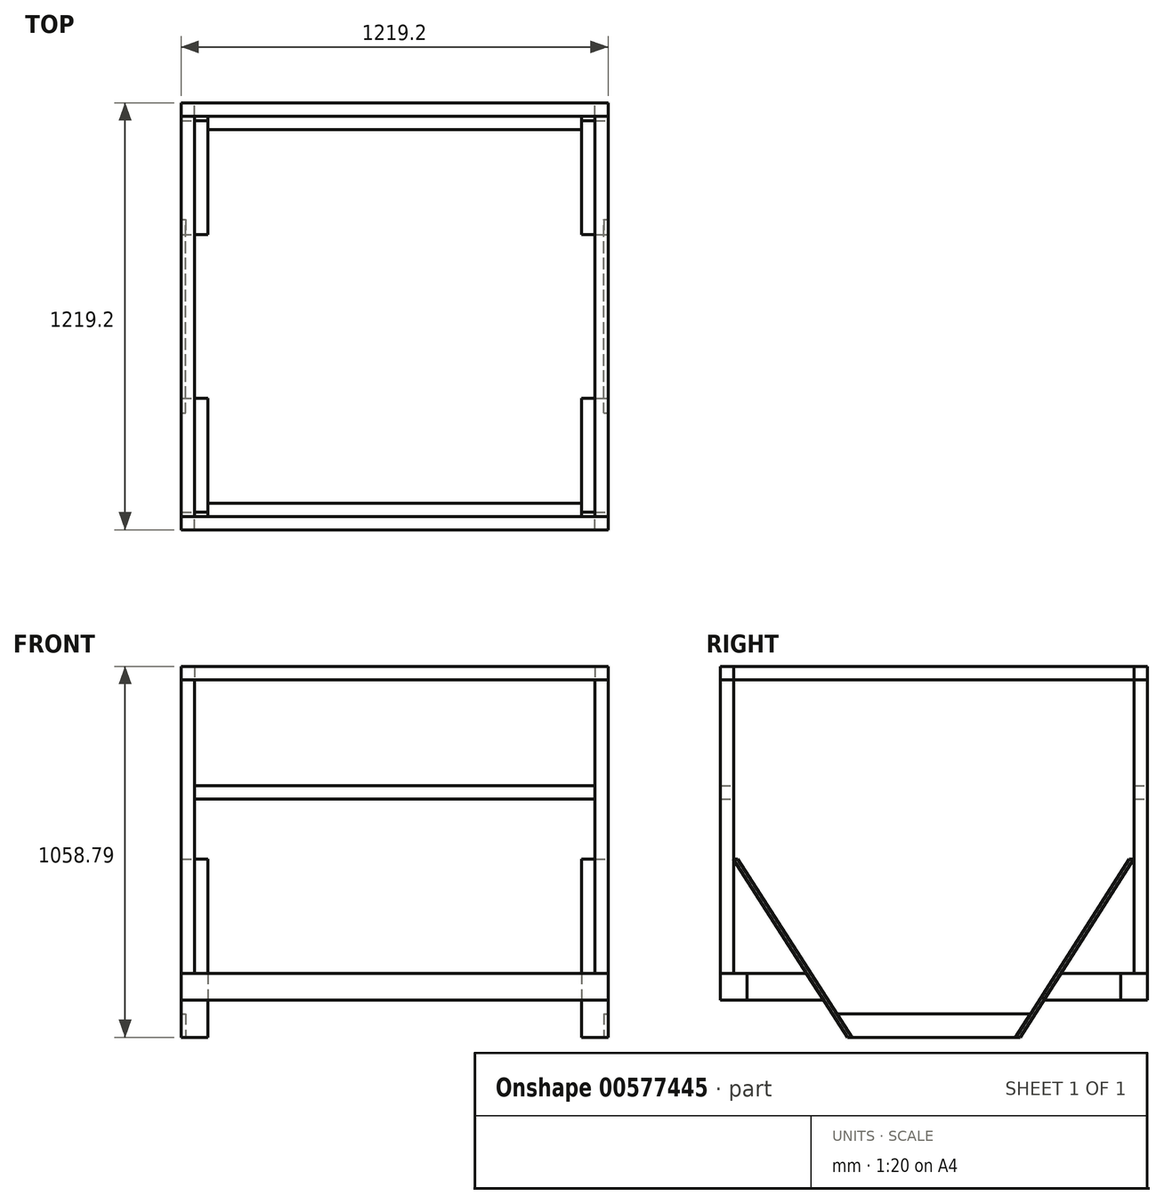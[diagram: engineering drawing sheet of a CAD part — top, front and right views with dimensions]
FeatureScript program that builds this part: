
annotation { "Feature Type Name" : "Feature", "Feature Type Description" : "" }
export const myFeature = defineFeature(function(context is Context, id is Id, definition is map)
    precondition{}
    {
        {
            var Q0;
            Q0=qCreatedBy(makeId("Front.planeOp"),FACE);
            var sketch = newSketch(context, id + "F0", { "sketchPlane" : qUnion([Q0])});
            skLineSegment(sketch, "E0.bottom", {"start": v(-609.6, 38.1) * mm, "end": v(609.6, 38.1) * mm});
            skLineSegment(sketch, "E0.top", {"start": v(-609.6, -38.1) * mm, "end": v(609.6, -38.1) * mm});
            skLineSegment(sketch, "E0.left", {"start": v(-609.6, 38.1) * mm, "end": v(-609.6, -38.1) * mm});
            skLineSegment(sketch, "E0.right", {"start": v(609.6, 38.1) * mm, "end": v(609.6, -38.1) * mm});
            skPoint(sketch, "E0.middle", {"position": v(0, 0) * mm});
            skSolve(sketch);
        }
        {
            var Q0;
            Q0=makeQuery(id+"F0.imprint","IMPRINT",FACE,{"disambiguationData":[TD([[makeQuery(id+"F0.imprint","IMPRINT",EDGE,{"derivedFrom":sQuery(id+"F0.wireOp",EDGE,"E0.bottom")}),-1.0]])]});
            extrude(context, id + "F1", {"entities" : qUnion([Q0]), "depth" : 76.2 * mm, "offsetDistance" : 25.4 * mm});
        }
        {
            var Q0;
            Q0=qCreatedBy(makeId("Front.planeOp"),FACE);
            var sketch = newSketch(context, id + "F2", { "sketchPlane" : qUnion([Q0])});
            skLineSegment(sketch, "E1.bottom", {"start": v(-609.6, 911.23) * mm, "end": v(609.6, 911.23) * mm});
            skLineSegment(sketch, "E1.top", {"start": v(-609.6, 873.12) * mm, "end": v(609.6, 873.12) * mm});
            skLineSegment(sketch, "E1.left", {"start": v(-609.6, 911.23) * mm, "end": v(-609.6, 873.12) * mm});
            skLineSegment(sketch, "E1.right", {"start": v(609.6, 911.23) * mm, "end": v(609.6, 873.12) * mm});
            skPoint(sketch, "E1.middle", {"position": v(0, 892.18) * mm});
            skSolve(sketch);
        }
        {
            var Q0;
            Q0=makeQuery(id+"F2.imprint","IMPRINT",FACE,{"disambiguationData":[TD([[makeQuery(id+"F2.imprint","IMPRINT",EDGE,{"derivedFrom":sQuery(id+"F2.wireOp",EDGE,"E1.bottom")}),-1.0]])]});
            extrude(context, id + "F3", {"entities" : qUnion([Q0]), "depth" : 38.1 * mm, "offsetDistance" : 25.4 * mm});
        }
        {
            var Q0;
            Q0=qCreatedBy(makeId("Front.planeOp"),FACE);
            var sketch = newSketch(context, id + "F4", { "sketchPlane" : qUnion([Q0])});
            skLineSegment(sketch, "E2.bottom", {"start": v(609.6, 876.3) * mm, "end": v(571.5, 876.3) * mm});
            skLineSegment(sketch, "E2.top", {"start": v(609.6, 38.1) * mm, "end": v(571.5, 38.1) * mm});
            skLineSegment(sketch, "E2.left", {"start": v(609.6, 876.3) * mm, "end": v(609.6, 38.1) * mm});
            skLineSegment(sketch, "E2.right", {"start": v(571.5, 876.3) * mm, "end": v(571.5, 38.1) * mm});
            skPoint(sketch, "E2.middle", {"position": v(590.55, 457.2) * mm});
            skSolve(sketch);
        }
        {
            var Q0;
            Q0=makeQuery(id+"F4.imprint","IMPRINT",FACE,{"disambiguationData":[TD([[makeQuery(id+"F4.imprint","IMPRINT",EDGE,{"derivedFrom":sQuery(id+"F4.wireOp",EDGE,"E2.bottom")}),1.0]])]});
            extrude(context, id + "F5", {"entities" : qUnion([Q0]), "depth" : 38.1 * mm, "offsetDistance" : 25.4 * mm});
        }
        {
            var Q0;
            Q0=makeQuery(id+"F5.opExtrude","SWEPT_BODY",BODY,{"disambiguationData":[OSD([sQuery(id+"F4.wireOp",EDGE,"E2.bottom"),sQuery(id+"F4.wireOp",EDGE,"E2.top"),sQuery(id+"F4.wireOp",EDGE,"E2.left"),sQuery(id+"F4.wireOp",EDGE,"E2.right")])]});
            var Q1;
            Q1=qCreatedBy(makeId("Right.planeOp"),FACE);
            transform(context, id + "F6", {"entities" : qUnion([Q0]), "transformType" : TransformType.TRANSLATION_DISTANCE, "transformDirection" : qUnion([Q1]), "distance" : 1181.1 * mm, "oppositeDirection" : true, "makeCopy" : true});
        }
        {
            var Q0;
            Q0=makeQuery(id+"F3.opExtrude","SWEPT_BODY",BODY,{"disambiguationData":[OSD([sQuery(id+"F2.wireOp",EDGE,"E1.bottom"),sQuery(id+"F2.wireOp",EDGE,"E1.top"),sQuery(id+"F2.wireOp",EDGE,"E1.left"),sQuery(id+"F2.wireOp",EDGE,"E1.right")])]});
            var Q1;
            Q1=qCreatedBy(makeId("Top.planeOp"),FACE);
            transform(context, id + "F7", {"entities" : qUnion([Q0]), "transformType" : TransformType.TRANSLATION_DISTANCE, "transformDirection" : qUnion([Q1]), "distance" : 3.17 * mm, "makeCopy" : false});
        }
        {
            var Q0;
            Q0=qCreatedBy(makeId("Front.planeOp"),FACE);
            var sketch = newSketch(context, id + "F8", { "sketchPlane" : qUnion([Q0])});
            skLineSegment(sketch, "E3.bottom", {"start": v(-571.5, 573.9) * mm, "end": v(571.5, 573.9) * mm});
            skLineSegment(sketch, "E3.top", {"start": v(-571.5, 535.8) * mm, "end": v(571.5, 535.8) * mm});
            skLineSegment(sketch, "E3.left", {"start": v(-571.5, 573.9) * mm, "end": v(-571.5, 535.8) * mm});
            skLineSegment(sketch, "E3.right", {"start": v(571.5, 573.9) * mm, "end": v(571.5, 535.8) * mm});
            skPoint(sketch, "E3.middle", {"position": v(0, 554.84) * mm});
            skSolve(sketch);
        }
        {
            var Q0;
            Q0=makeQuery(id+"F8.imprint","IMPRINT",FACE,{"disambiguationData":[TD([[makeQuery(id+"F8.imprint","IMPRINT",EDGE,{"derivedFrom":sQuery(id+"F8.wireOp",EDGE,"E3.bottom")}),-1.0]])]});
            extrude(context, id + "F9", {"entities" : qUnion([Q0]), "depth" : 38.1 * mm, "offsetDistance" : 25.4 * mm});
        }
        {
            var Q0;
            Q0=makeQuery(id+"F6.opPattern","COPY",BODY,{"derivedFrom":makeQuery(id+"F5.opExtrude","SWEPT_BODY",BODY,{"disambiguationData":[OSD([sQuery(id+"F4.wireOp",EDGE,"E2.bottom"),sQuery(id+"F4.wireOp",EDGE,"E2.top"),sQuery(id+"F4.wireOp",EDGE,"E2.left"),sQuery(id+"F4.wireOp",EDGE,"E2.right")])]}),"instanceName":"1"});
            var Q1;
            Q1=makeQuery(id+"F3.opExtrude","SWEPT_BODY",BODY,{"disambiguationData":[OSD([sQuery(id+"F2.wireOp",EDGE,"E1.bottom"),sQuery(id+"F2.wireOp",EDGE,"E1.top"),sQuery(id+"F2.wireOp",EDGE,"E1.left"),sQuery(id+"F2.wireOp",EDGE,"E1.right")])]});
            var Q2;
            Q2=makeQuery(id+"F9.opExtrude","SWEPT_BODY",BODY,{"disambiguationData":[OSD([sQuery(id+"F8.wireOp",EDGE,"E3.bottom"),sQuery(id+"F8.wireOp",EDGE,"E3.top"),sQuery(id+"F8.wireOp",EDGE,"E3.left"),sQuery(id+"F8.wireOp",EDGE,"E3.right")])]});
            var Q3;
            Q3=makeQuery(id+"F5.opExtrude","SWEPT_BODY",BODY,{"disambiguationData":[OSD([sQuery(id+"F4.wireOp",EDGE,"E2.bottom"),sQuery(id+"F4.wireOp",EDGE,"E2.top"),sQuery(id+"F4.wireOp",EDGE,"E2.left"),sQuery(id+"F4.wireOp",EDGE,"E2.right")])]});
            var Q4;
            Q4=qCreatedBy(makeId("Front.planeOp"),FACE);
            transform(context, id + "F10", {"entities" : qUnion([Q0, Q1, Q2, Q3]), "transformType" : TransformType.TRANSLATION_DISTANCE, "transformDirection" : qUnion([Q4]), "distance" : 38.1 * mm, "makeCopy" : false});
        }
        {
            var Q0;
            Q0=makeQuery(id+"F1.opExtrude","SWEPT_BODY",BODY,{"disambiguationData":[OSD([sQuery(id+"F0.wireOp",EDGE,"E0.bottom"),sQuery(id+"F0.wireOp",EDGE,"E0.top"),sQuery(id+"F0.wireOp",EDGE,"E0.left"),sQuery(id+"F0.wireOp",EDGE,"E0.right")])]});
            var Q1;
            Q1=makeQuery(id+"F3.opExtrude","SWEPT_BODY",BODY,{"disambiguationData":[OSD([sQuery(id+"F2.wireOp",EDGE,"E1.bottom"),sQuery(id+"F2.wireOp",EDGE,"E1.top"),sQuery(id+"F2.wireOp",EDGE,"E1.left"),sQuery(id+"F2.wireOp",EDGE,"E1.right")])]});
            var Q2;
            Q2=makeQuery(id+"F5.opExtrude","SWEPT_BODY",BODY,{"disambiguationData":[OSD([sQuery(id+"F4.wireOp",EDGE,"E2.bottom"),sQuery(id+"F4.wireOp",EDGE,"E2.top"),sQuery(id+"F4.wireOp",EDGE,"E2.left"),sQuery(id+"F4.wireOp",EDGE,"E2.right")])]});
            var Q3;
            Q3=makeQuery(id+"F9.opExtrude","SWEPT_BODY",BODY,{"disambiguationData":[OSD([sQuery(id+"F8.wireOp",EDGE,"E3.bottom"),sQuery(id+"F8.wireOp",EDGE,"E3.top"),sQuery(id+"F8.wireOp",EDGE,"E3.left"),sQuery(id+"F8.wireOp",EDGE,"E3.right")])]});
            var Q4;
            Q4=makeQuery(id+"F6.opPattern","COPY",BODY,{"derivedFrom":makeQuery(id+"F5.opExtrude","SWEPT_BODY",BODY,{"disambiguationData":[OSD([sQuery(id+"F4.wireOp",EDGE,"E2.bottom"),sQuery(id+"F4.wireOp",EDGE,"E2.top"),sQuery(id+"F4.wireOp",EDGE,"E2.left"),sQuery(id+"F4.wireOp",EDGE,"E2.right")])]}),"instanceName":"1"});
            var Q5;
            Q5=qCreatedBy(makeId("Front.planeOp"),FACE);
            transform(context, id + "F11", {"entities" : qUnion([Q0, Q1, Q2, Q3, Q4]), "transformType" : TransformType.TRANSLATION_DISTANCE, "transformDirection" : qUnion([Q5]), "distance" : 1143 * mm, "oppositeDirection" : true, "makeCopy" : true});
        }
        {
            var Q0;
            Q0=makeQuery(id+"F11.opPattern","COPY",BODY,{"derivedFrom":makeQuery(id+"F9.opExtrude","SWEPT_BODY",BODY,{"disambiguationData":[OSD([sQuery(id+"F8.wireOp",EDGE,"E3.bottom"),sQuery(id+"F8.wireOp",EDGE,"E3.top"),sQuery(id+"F8.wireOp",EDGE,"E3.left"),sQuery(id+"F8.wireOp",EDGE,"E3.right")])]}),"instanceName":"1"});
            var Q1;
            Q1=makeQuery(id+"F11.opPattern","COPY",BODY,{"derivedFrom":makeQuery(id+"F6.opPattern","COPY",BODY,{"derivedFrom":makeQuery(id+"F5.opExtrude","SWEPT_BODY",BODY,{"disambiguationData":[OSD([sQuery(id+"F4.wireOp",EDGE,"E2.bottom"),sQuery(id+"F4.wireOp",EDGE,"E2.top"),sQuery(id+"F4.wireOp",EDGE,"E2.left"),sQuery(id+"F4.wireOp",EDGE,"E2.right")])]}),"instanceName":"1"}),"instanceName":"1"});
            var Q2;
            Q2=makeQuery(id+"F11.opPattern","COPY",BODY,{"derivedFrom":makeQuery(id+"F3.opExtrude","SWEPT_BODY",BODY,{"disambiguationData":[OSD([sQuery(id+"F2.wireOp",EDGE,"E1.bottom"),sQuery(id+"F2.wireOp",EDGE,"E1.top"),sQuery(id+"F2.wireOp",EDGE,"E1.left"),sQuery(id+"F2.wireOp",EDGE,"E1.right")])]}),"instanceName":"1"});
            var Q3;
            Q3=makeQuery(id+"F11.opPattern","COPY",BODY,{"derivedFrom":makeQuery(id+"F5.opExtrude","SWEPT_BODY",BODY,{"disambiguationData":[OSD([sQuery(id+"F4.wireOp",EDGE,"E2.bottom"),sQuery(id+"F4.wireOp",EDGE,"E2.top"),sQuery(id+"F4.wireOp",EDGE,"E2.left"),sQuery(id+"F4.wireOp",EDGE,"E2.right")])]}),"instanceName":"1"});
            var Q4;
            Q4=qCreatedBy(makeId("Front.planeOp"),FACE);
            transform(context, id + "F12", {"entities" : qUnion([Q0, Q1, Q2, Q3]), "transformType" : TransformType.TRANSLATION_DISTANCE, "transformDirection" : qUnion([Q4]), "distance" : 38.1 * mm, "oppositeDirection" : true, "makeCopy" : false});
        }
        {
            var Q0;
            Q0=makeQuery(id+"F3.opExtrude","SWEPT_FACE",FACE,{"disambiguationData":[OSD([sQuery(id+"F2.wireOp",EDGE,"E1.right")])]});
            var sketch = newSketch(context, id + "F13", { "sketchPlane" : qUnion([Q0])});
            skLineSegment(sketch, "E4.bottom", {"start": v(-38.1, 914.4) * mm, "end": v(1104.9, 914.4) * mm});
            skLineSegment(sketch, "E4.top", {"start": v(-38.1, 876.3) * mm, "end": v(1104.9, 876.3) * mm});
            skLineSegment(sketch, "E4.left", {"start": v(-38.1, 914.4) * mm, "end": v(-38.1, 876.3) * mm});
            skLineSegment(sketch, "E4.right", {"start": v(1104.9, 914.4) * mm, "end": v(1104.9, 876.3) * mm});
            skSolve(sketch);
        }
        {
            var Q0;
            Q0=makeQuery(id+"F13.imprint","IMPRINT",FACE,{"disambiguationData":[TD([[makeQuery(id+"F13.imprint","IMPRINT",EDGE,{"derivedFrom":sQuery(id+"F13.wireOp",EDGE,"E4.bottom")}),-1.0]])]});
            extrude(context, id + "F14", {"entities" : qUnion([Q0]), "oppositeDirection" : true, "depth" : 38.1 * mm, "offsetDistance" : 25.4 * mm});
        }
        {
            var Q0;
            Q0=makeQuery(id+"F14.opExtrude","SWEPT_BODY",BODY,{"disambiguationData":[OSD([sQuery(id+"F13.wireOp",EDGE,"E4.bottom"),sQuery(id+"F13.wireOp",EDGE,"E4.top"),sQuery(id+"F13.wireOp",EDGE,"E4.left"),sQuery(id+"F13.wireOp",EDGE,"E4.right")])]});
            var Q1;
            Q1=qCreatedBy(makeId("Right.planeOp"),FACE);
            transform(context, id + "F15", {"entities" : qUnion([Q0]), "transformType" : TransformType.TRANSLATION_DISTANCE, "transformDirection" : qUnion([Q1]), "distance" : 1181.1 * mm, "oppositeDirection" : true, "makeCopy" : true});
        }
        {
            var Q0;
            Q0=makeQuery(id+"F11.opPattern","COPY",FACE,{"derivedFrom":makeQuery(id+"F1.opExtrude","SWEPT_FACE",FACE,{"disambiguationData":[OSD([sQuery(id+"F0.wireOp",EDGE,"E0.right")])]}),"instanceName":"1"});
            var sketch = newSketch(context, id + "F16", { "sketchPlane" : qUnion([Q0])});
            skLineSegment(sketch, "E5", {"start": v(1066.8, -38.1) * mm, "end": v(847.72, -38.1) * mm});
            skLineSegment(sketch, "E6", {"start": v(1066.8, 38.1) * mm, "end": v(896.92, 38.1) * mm});
            skLineSegment(sketch, "E7", {"start": v(896.92, 38.1) * mm, "end": v(847.72, -38.1) * mm});
            skSolve(sketch);
        }
        {
            var Q0;
            Q0=makeQuery(id+"F16.imprint","IMPRINT",FACE,{"disambiguationData":[TD([[makeQuery(id+"F16.imprint","IMPRINT",EDGE,{"derivedFrom":sQuery(id+"F16.wireOp",EDGE,"E5")}),-1.0]])]});
            extrude(context, id + "F17", {"entities" : qUnion([Q0]), "oppositeDirection" : true, "depth" : 76.2 * mm, "offsetDistance" : 25.4 * mm});
        }
        {
            var Q0;
            Q0=makeQuery(id+"F1.opExtrude","SWEPT_FACE",FACE,{"disambiguationData":[OSD([sQuery(id+"F0.wireOp",EDGE,"E0.right")])]});
            var sketch = newSketch(context, id + "F18", { "sketchPlane" : qUnion([Q0])});
            skLineSegment(sketch, "E8", {"start": v(0, -38.1) * mm, "end": v(219.08, -38.1) * mm});
            skLineSegment(sketch, "E9", {"start": v(0, 38.1) * mm, "end": v(169.88, 38.1) * mm});
            skLineSegment(sketch, "E10", {"start": v(169.88, 38.1) * mm, "end": v(219.08, -38.1) * mm});
            skSolve(sketch);
        }
        {
            var Q0;
            Q0=makeQuery(id+"F18.imprint","IMPRINT",FACE,{"disambiguationData":[TD([[makeQuery(id+"F18.imprint","IMPRINT",EDGE,{"derivedFrom":sQuery(id+"F18.wireOp",EDGE,"E8")}),1.0]])]});
            extrude(context, id + "F19", {"entities" : qUnion([Q0]), "oppositeDirection" : true, "depth" : 76.2 * mm, "offsetDistance" : 25.4 * mm});
        }
        {
            var Q0;
            Q0=makeQuery(id+"F17.opExtrude","SWEPT_BODY",BODY,{"disambiguationData":[OSD([sQuery(id+"F0.wireOp",EDGE,"E0.right"),sQuery(id+"F16.wireOp",EDGE,"E5"),sQuery(id+"F16.wireOp",EDGE,"E6"),sQuery(id+"F16.wireOp",EDGE,"E7")])]});
            var Q1;
            Q1=makeQuery(id+"F19.opExtrude","SWEPT_BODY",BODY,{"disambiguationData":[OSD([sQuery(id+"F0.wireOp",EDGE,"E0.right"),sQuery(id+"F18.wireOp",EDGE,"E8"),sQuery(id+"F18.wireOp",EDGE,"E9"),sQuery(id+"F18.wireOp",EDGE,"E10")])]});
            var Q2;
            Q2=qCreatedBy(makeId("Right.planeOp"),FACE);
            transform(context, id + "F20", {"entities" : qUnion([Q0, Q1]), "transformType" : TransformType.TRANSLATION_DISTANCE, "transformDirection" : qUnion([Q2]), "distance" : 1143 * mm, "oppositeDirection" : true, "makeCopy" : true});
        }
        {
            var Q0;
            Q0=makeQuery(id+"F19.opExtrude","CAP_FACE",FACE,{"disambiguationData":[OSD([sQuery(id+"F0.wireOp",EDGE,"E0.right"),sQuery(id+"F18.wireOp",EDGE,"E8"),sQuery(id+"F18.wireOp",EDGE,"E9"),sQuery(id+"F18.wireOp",EDGE,"E10")])],"isStart":true});
            var sketch = newSketch(context, id + "F21", { "sketchPlane" : qUnion([Q0])});
            skLineSegment(sketch, "E11", {"start": v(257.18, -77.77) * mm, "end": v(809.63, -77.77) * mm});
            skLineSegment(sketch, "E12", {"start": v(300.02, -144.39) * mm, "end": v(766.75, -144.39) * mm});
            skLineSegment(sketch, "E13", {"start": v(809.63, -77.77) * mm, "end": v(766.75, -144.39) * mm});
            skLineSegment(sketch, "E14", {"start": v(257.18, -77.77) * mm, "end": v(300.02, -144.39) * mm});
            skSolve(sketch);
        }
        {
            var Q0;
            Q0=makeQuery(id+"F21.imprint","IMPRINT",FACE,{"disambiguationData":[TD([[makeQuery(id+"F21.imprint","IMPRINT",EDGE,{"derivedFrom":sQuery(id+"F21.wireOp",EDGE,"E11")}),-1.0]])]});
            extrude(context, id + "F22", {"entities" : qUnion([Q0]), "oppositeDirection" : true, "depth" : 12.7 * mm, "offsetDistance" : 25.4 * mm});
        }
        {
            var Q0;
            Q0=makeQuery(id+"F11.opPattern","COPY",FACE,{"derivedFrom":makeQuery(id+"F1.opExtrude","SWEPT_FACE",FACE,{"disambiguationData":[OSD([sQuery(id+"F0.wireOp",EDGE,"E0.right")])]}),"instanceName":"1"});
            var sketch = newSketch(context, id + "F23", { "sketchPlane" : qUnion([Q0])});
            skLineSegment(sketch, "E15", {"start": v(779.87, -144.36) * mm, "end": v(1104.63, 364.2) * mm});
            skLineSegment(sketch, "E16", {"start": v(767.17, -144.36) * mm, "end": v(779.87, -144.36) * mm});
            skLineSegment(sketch, "E17", {"start": v(1091.93, 364.2) * mm, "end": v(767.17, -144.36) * mm});
            skLineSegment(sketch, "E18", {"start": v(1104.63, 364.2) * mm, "end": v(1091.93, 364.2) * mm});
            skSolve(sketch);
        }
        {
            var Q0;
            Q0=makeQuery(id+"F23.imprint","IMPRINT",FACE,{"disambiguationData":[TD([[makeQuery(id+"F23.imprint","IMPRINT",EDGE,{"derivedFrom":sQuery(id+"F23.wireOp",EDGE,"E15")}),1.0]])]});
            extrude(context, id + "F24", {"entities" : qUnion([Q0]), "oppositeDirection" : true, "depth" : 76.2 * mm, "offsetDistance" : 25.4 * mm});
        }
        {
            var Q0;
            Q0=makeQuery(id+"F1.opExtrude","SWEPT_FACE",FACE,{"disambiguationData":[OSD([sQuery(id+"F0.wireOp",EDGE,"E0.right")])]});
            var sketch = newSketch(context, id + "F25", { "sketchPlane" : qUnion([Q0])});
            skLineSegment(sketch, "E19", {"start": v(-38.38, 364.21) * mm, "end": v(-25.68, 364.21) * mm});
            skLineSegment(sketch, "E20", {"start": v(287.23, -144.35) * mm, "end": v(299.94, -144.35) * mm});
            skLineSegment(sketch, "E21", {"start": v(299.94, -144.35) * mm, "end": v(-25.68, 364.21) * mm});
            skLineSegment(sketch, "E22", {"start": v(-38.38, 364.21) * mm, "end": v(287.23, -144.35) * mm});
            skSolve(sketch);
        }
        {
            var Q0;
            Q0=makeQuery(id+"F25.imprint","IMPRINT",FACE,{"disambiguationData":[TD([[makeQuery(id+"F25.imprint","IMPRINT",EDGE,{"derivedFrom":sQuery(id+"F25.wireOp",EDGE,"E19")}),-1.0]])]});
            extrude(context, id + "F26", {"entities" : qUnion([Q0]), "oppositeDirection" : true, "depth" : 76.2 * mm, "offsetDistance" : 25.4 * mm});
        }
        {
            var Q0;
            Q0=makeQuery(id+"F22.opExtrude","SWEPT_BODY",BODY,{"disambiguationData":[OSD([sQuery(id+"F21.wireOp",EDGE,"E11"),sQuery(id+"F21.wireOp",EDGE,"E12"),sQuery(id+"F21.wireOp",EDGE,"E13"),sQuery(id+"F21.wireOp",EDGE,"E14")])]});
            var Q1;
            Q1=makeQuery(id+"F24.opExtrude","SWEPT_BODY",BODY,{"disambiguationData":[OSD([sQuery(id+"F23.wireOp",EDGE,"E15"),sQuery(id+"F23.wireOp",EDGE,"E16"),sQuery(id+"F23.wireOp",EDGE,"E17"),sQuery(id+"F23.wireOp",EDGE,"E18")])]});
            var Q2;
            Q2=makeQuery(id+"F26.opExtrude","SWEPT_BODY",BODY,{"disambiguationData":[OSD([sQuery(id+"F25.wireOp",EDGE,"E19"),sQuery(id+"F25.wireOp",EDGE,"E20"),sQuery(id+"F25.wireOp",EDGE,"E21"),sQuery(id+"F25.wireOp",EDGE,"E22")])]});
            var Q3;
            Q3=qCreatedBy(makeId("Right.planeOp"),FACE);
            transform(context, id + "F27", {"entities" : qUnion([Q0, Q1, Q2]), "transformType" : TransformType.TRANSLATION_DISTANCE, "transformDirection" : qUnion([Q3]), "distance" : 1143 * mm, "oppositeDirection" : true, "makeCopy" : true});
        }
        {
            var Q0;
            Q0=makeQuery(id+"F27.opPattern","COPY",BODY,{"derivedFrom":makeQuery(id+"F22.opExtrude","SWEPT_BODY",BODY,{"disambiguationData":[OSD([sQuery(id+"F21.wireOp",EDGE,"E11"),sQuery(id+"F21.wireOp",EDGE,"E12"),sQuery(id+"F21.wireOp",EDGE,"E13"),sQuery(id+"F21.wireOp",EDGE,"E14")])]}),"instanceName":"1"});
            var Q1;
            Q1=qCreatedBy(makeId("Right.planeOp"),FACE);
            transform(context, id + "F28", {"entities" : qUnion([Q0]), "transformType" : TransformType.TRANSLATION_DISTANCE, "transformDirection" : qUnion([Q1]), "distance" : 63.5 * mm, "oppositeDirection" : true, "makeCopy" : false});
        }
    });
